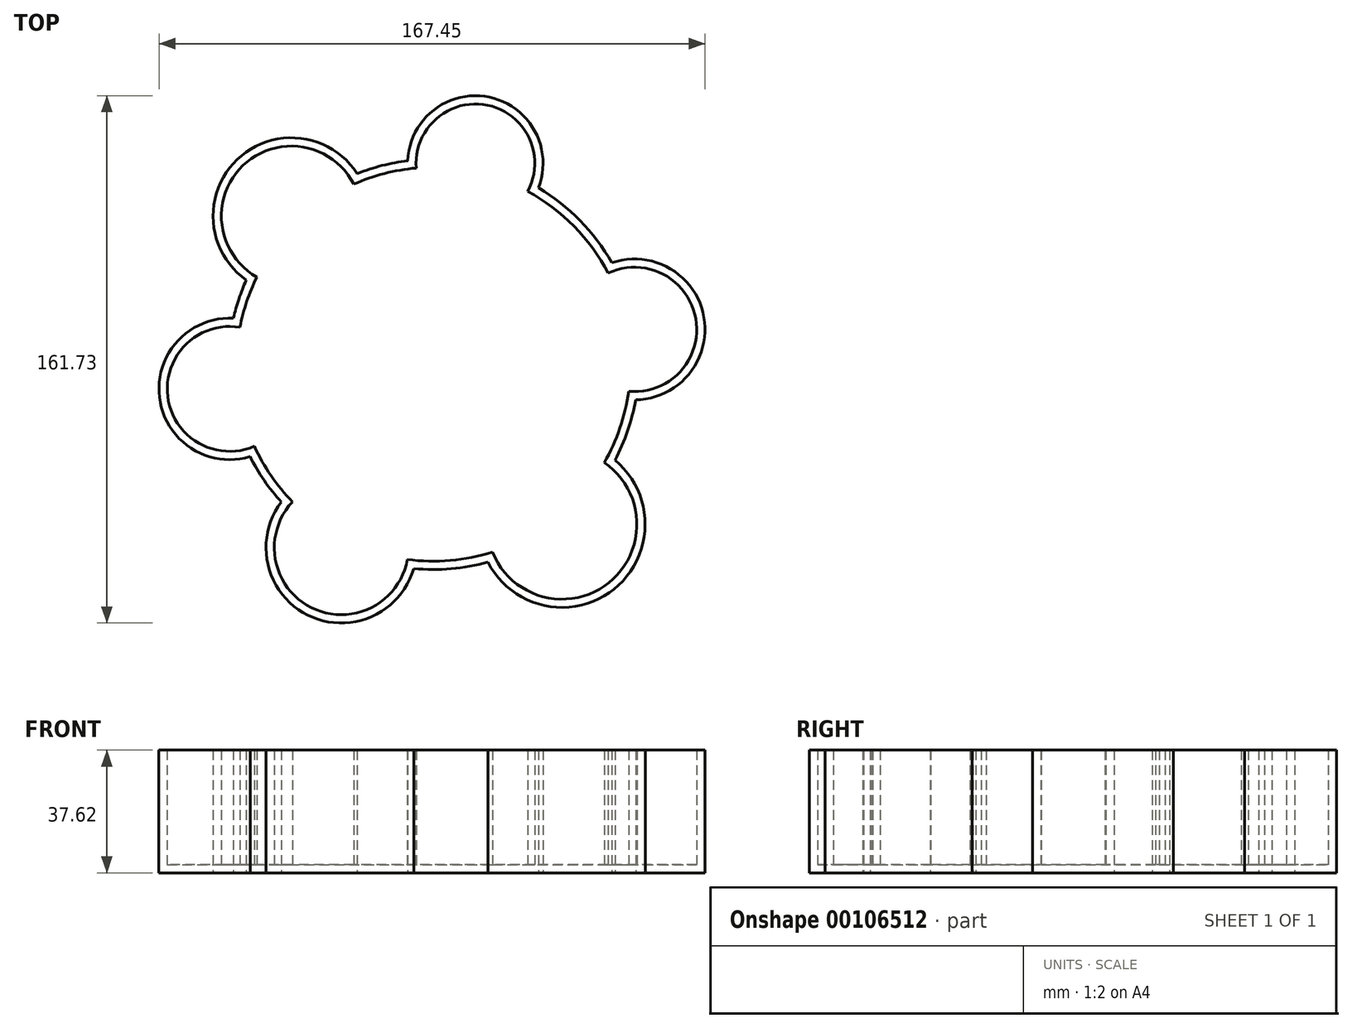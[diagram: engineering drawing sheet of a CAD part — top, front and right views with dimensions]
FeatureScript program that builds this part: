
annotation { "Feature Type Name" : "Feature", "Feature Type Description" : "" }
export const myFeature = defineFeature(function(context is Context, id is Id, definition is map)
    precondition{}
    {
        {
            var Q0;
            Q0=qCreatedBy(makeId("Top.planeOp"),FACE);
            var sketch = newSketch(context, id + "F0", { "sketchPlane" : qUnion([Q0])});
            skCircle(sketch, "E0", {"center": v(0, 0) * mm, "radius": 62.96 * mm});
            skCircle(sketch, "E1", {"center": v(61.65, 10.7) * mm, "radius": 21.6 * mm});
            skCircle(sketch, "E2", {"center": v(12.86, 61.63) * mm, "radius": 20.74 * mm});
            skCircle(sketch, "E3", {"center": v(-43.56, 45.45) * mm, "radius": 24.02 * mm});
            skCircle(sketch, "E4", {"center": v(-62.5, -7.56) * mm, "radius": 21.7 * mm});
            skCircle(sketch, "E5", {"center": v(-28.25, -56.26) * mm, "radius": 23.1 * mm});
            skCircle(sketch, "E6", {"center": v(39.41, -49.1) * mm, "radius": 25.5 * mm});
            skSolve(sketch);
        }
        {
            var Q0;
            {var subQ0=sQuery(id+"F0.wireOp",EDGE,"E6");var subQ1=sQuery(id+"F0.wireOp",EDGE,"E0");var subQ2=makeQuery(id+"F0.imprint","INTERSECT",VERTEX,{"disambiguationData":[OD(0.0)],"derivedFrom":[subQ1,subQ0]});Q0=makeQuery(id+"F0.imprint","IMPRINT",FACE,{"disambiguationData":[TD([[makeQuery(id+"F0.imprint","IMPRINT",EDGE,{"disambiguationData":[TD([[subQ2,-1.0]])],"derivedFrom":subQ1}),1.0]])]});}
            var Q1;
            {var subQ1=sQuery(id+"F0.wireOp",EDGE,"E0");var subQ7=sQuery(id+"F0.wireOp",EDGE,"E2");var subQ8=makeQuery(id+"F0.imprint","INTERSECT",VERTEX,{"disambiguationData":[OD(0.0)],"derivedFrom":[subQ1,subQ7]});Q1=makeQuery(id+"F0.imprint","IMPRINT",FACE,{"disambiguationData":[TD([[makeQuery(id+"F0.imprint","IMPRINT",EDGE,{"disambiguationData":[TD([[subQ8,1.0]])],"derivedFrom":subQ1}),1.0]])]});}
            var Q2;
            {var subQ0=sQuery(id+"F0.wireOp",EDGE,"E1");var subQ1=sQuery(id+"F0.wireOp",EDGE,"E0");var subQ2=makeQuery(id+"F0.imprint","INTERSECT",VERTEX,{"disambiguationData":[OD(0.0)],"derivedFrom":[subQ1,subQ0]});Q2=makeQuery(id+"F0.imprint","IMPRINT",FACE,{"disambiguationData":[TD([[makeQuery(id+"F0.imprint","IMPRINT",EDGE,{"disambiguationData":[TD([[subQ2,1.0]])],"derivedFrom":subQ1}),1.0]])]});}
            var Q3;
            {var subQ0=sQuery(id+"F0.wireOp",EDGE,"E5");var subQ1=sQuery(id+"F0.wireOp",EDGE,"E0");var subQ2=makeQuery(id+"F0.imprint","INTERSECT",VERTEX,{"disambiguationData":[OD(0.0)],"derivedFrom":[subQ1,subQ0]});Q3=makeQuery(id+"F0.imprint","IMPRINT",FACE,{"disambiguationData":[TD([[makeQuery(id+"F0.imprint","IMPRINT",EDGE,{"disambiguationData":[TD([[subQ2,-1.0]])],"derivedFrom":subQ1}),1.0]])]});}
            var Q4;
            {var subQ0=sQuery(id+"F0.wireOp",EDGE,"E3");var subQ1=sQuery(id+"F0.wireOp",EDGE,"E0");var subQ2=makeQuery(id+"F0.imprint","INTERSECT",VERTEX,{"disambiguationData":[OD(0.0)],"derivedFrom":[subQ1,subQ0]});Q4=makeQuery(id+"F0.imprint","IMPRINT",FACE,{"disambiguationData":[TD([[makeQuery(id+"F0.imprint","IMPRINT",EDGE,{"disambiguationData":[TD([[subQ2,-1.0]])],"derivedFrom":subQ1}),-1.0]])]});}
            var Q5;
            {var subQ0=sQuery(id+"F0.wireOp",EDGE,"E4");var subQ1=sQuery(id+"F0.wireOp",EDGE,"E0");var subQ2=makeQuery(id+"F0.imprint","INTERSECT",VERTEX,{"disambiguationData":[OD(0.0)],"derivedFrom":[subQ1,subQ0]});Q5=makeQuery(id+"F0.imprint","IMPRINT",FACE,{"disambiguationData":[TD([[makeQuery(id+"F0.imprint","IMPRINT",EDGE,{"disambiguationData":[TD([[subQ2,-1.0]])],"derivedFrom":subQ1}),1.0]])]});}
            var Q6;
            {var subQ0=sQuery(id+"F0.wireOp",EDGE,"E4");var subQ1=sQuery(id+"F0.wireOp",EDGE,"E0");var subQ2=makeQuery(id+"F0.imprint","INTERSECT",VERTEX,{"disambiguationData":[OD(0.0)],"derivedFrom":[subQ1,subQ0]});Q6=makeQuery(id+"F0.imprint","IMPRINT",FACE,{"disambiguationData":[TD([[makeQuery(id+"F0.imprint","IMPRINT",EDGE,{"disambiguationData":[TD([[subQ2,-1.0]])],"derivedFrom":subQ1}),-1.0]])]});}
            var Q7;
            {var subQ0=sQuery(id+"F0.wireOp",EDGE,"E2");var subQ1=sQuery(id+"F0.wireOp",EDGE,"E0");var subQ2=makeQuery(id+"F0.imprint","INTERSECT",VERTEX,{"disambiguationData":[OD(0.0)],"derivedFrom":[subQ1,subQ0]});Q7=makeQuery(id+"F0.imprint","IMPRINT",FACE,{"disambiguationData":[TD([[makeQuery(id+"F0.imprint","IMPRINT",EDGE,{"disambiguationData":[TD([[subQ2,-1.0]])],"derivedFrom":subQ1}),-1.0]])]});}
            var Q8;
            {var subQ0=sQuery(id+"F0.wireOp",EDGE,"E3");var subQ1=sQuery(id+"F0.wireOp",EDGE,"E0");var subQ2=makeQuery(id+"F0.imprint","INTERSECT",VERTEX,{"disambiguationData":[OD(0.0)],"derivedFrom":[subQ1,subQ0]});Q8=makeQuery(id+"F0.imprint","IMPRINT",FACE,{"disambiguationData":[TD([[makeQuery(id+"F0.imprint","IMPRINT",EDGE,{"disambiguationData":[TD([[subQ2,-1.0]])],"derivedFrom":subQ1}),1.0]])]});}
            var Q9;
            {var subQ0=sQuery(id+"F0.wireOp",EDGE,"E6");var subQ1=sQuery(id+"F0.wireOp",EDGE,"E0");var subQ2=makeQuery(id+"F0.imprint","INTERSECT",VERTEX,{"disambiguationData":[OD(0.0)],"derivedFrom":[subQ1,subQ0]});Q9=makeQuery(id+"F0.imprint","IMPRINT",FACE,{"disambiguationData":[TD([[makeQuery(id+"F0.imprint","IMPRINT",EDGE,{"disambiguationData":[TD([[subQ2,-1.0]])],"derivedFrom":subQ1}),-1.0]])]});}
            var Q10;
            {var subQ0=sQuery(id+"F0.wireOp",EDGE,"E1");var subQ1=sQuery(id+"F0.wireOp",EDGE,"E0");var subQ2=makeQuery(id+"F0.imprint","INTERSECT",VERTEX,{"disambiguationData":[OD(0.0)],"derivedFrom":[subQ1,subQ0]});Q10=makeQuery(id+"F0.imprint","IMPRINT",FACE,{"disambiguationData":[TD([[makeQuery(id+"F0.imprint","IMPRINT",EDGE,{"disambiguationData":[TD([[subQ2,1.0]])],"derivedFrom":subQ1}),-1.0]])]});}
            var Q11;
            {var subQ0=sQuery(id+"F0.wireOp",EDGE,"E5");var subQ1=sQuery(id+"F0.wireOp",EDGE,"E0");var subQ2=makeQuery(id+"F0.imprint","INTERSECT",VERTEX,{"disambiguationData":[OD(0.0)],"derivedFrom":[subQ1,subQ0]});Q11=makeQuery(id+"F0.imprint","IMPRINT",FACE,{"disambiguationData":[TD([[makeQuery(id+"F0.imprint","IMPRINT",EDGE,{"disambiguationData":[TD([[subQ2,-1.0]])],"derivedFrom":subQ1}),-1.0]])]});}
            var Q12;
            {var subQ0=sQuery(id+"F0.wireOp",EDGE,"E2");var subQ1=sQuery(id+"F0.wireOp",EDGE,"E0");var subQ2=makeQuery(id+"F0.imprint","INTERSECT",VERTEX,{"disambiguationData":[OD(0.0)],"derivedFrom":[subQ1,subQ0]});Q12=makeQuery(id+"F0.imprint","IMPRINT",FACE,{"disambiguationData":[TD([[makeQuery(id+"F0.imprint","IMPRINT",EDGE,{"disambiguationData":[TD([[subQ2,-1.0]])],"derivedFrom":subQ1}),1.0]])]});}
            extrude(context, id + "F1", {"entities" : qUnion([Q0, Q1, Q2, Q3, Q4, Q5, Q6, Q7, Q8, Q9, Q10, Q11, Q12]), "depth" : 37.62 * mm});
        }
        {
            var Q0;
            Q0=makeQuery(id+"F1.opExtrude","CAP_FACE",FACE,{"disambiguationData":[OSD([sQuery(id+"F0.wireOp",EDGE,"E0"),sQuery(id+"F0.wireOp",EDGE,"E1"),sQuery(id+"F0.wireOp",EDGE,"E2"),sQuery(id+"F0.wireOp",EDGE,"E3"),sQuery(id+"F0.wireOp",EDGE,"E4"),sQuery(id+"F0.wireOp",EDGE,"E5"),sQuery(id+"F0.wireOp",EDGE,"E6")])],"isStart":false});
            shell(context, id + "F2", {"entities" : qUnion([Q0]), "thickness" : 2.54 * mm});
        }
    });
